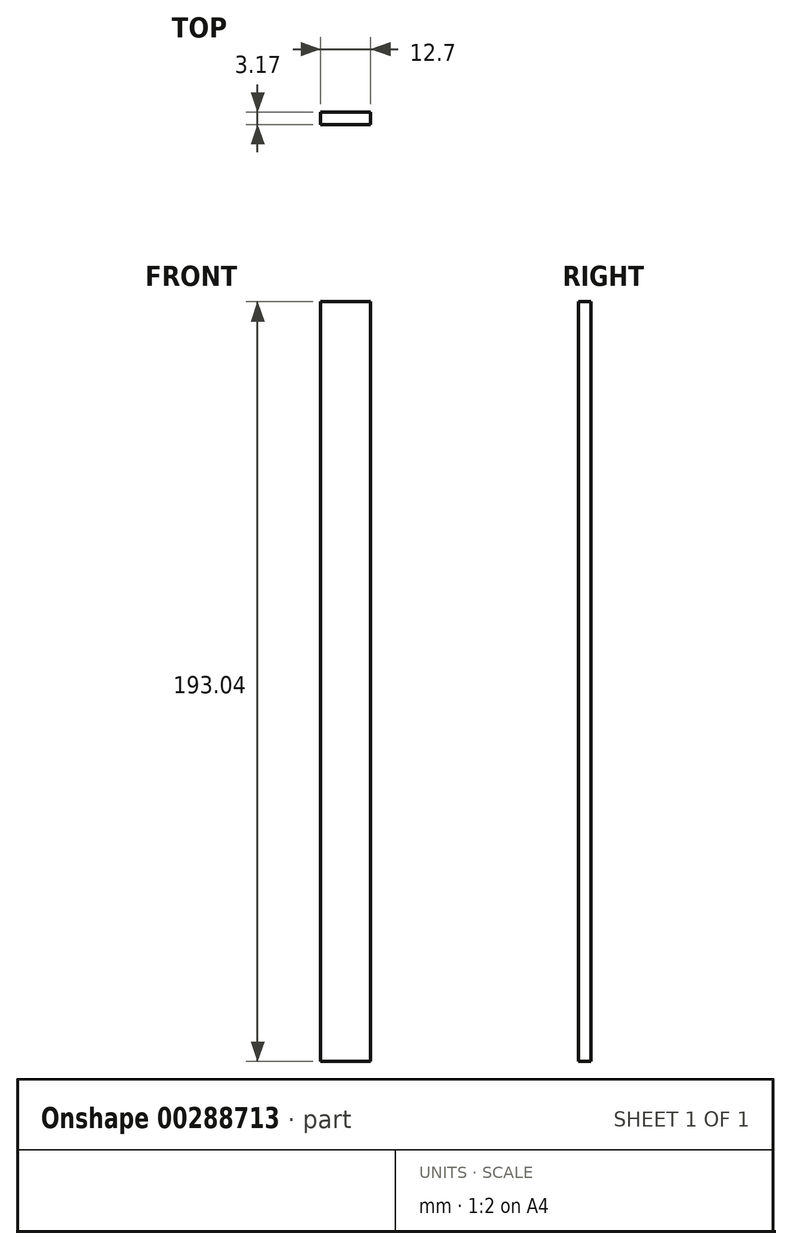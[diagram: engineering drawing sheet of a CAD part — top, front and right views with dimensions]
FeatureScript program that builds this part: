
annotation { "Feature Type Name" : "Feature", "Feature Type Description" : "" }
export const myFeature = defineFeature(function(context is Context, id is Id, definition is map)
    precondition{}
    {
        {
            var Q0;
            Q0=qCreatedBy(makeId("Front.planeOp"),FACE);
            var sketch = newSketch(context, id + "F0", { "sketchPlane" : qUnion([Q0])});
            skLineSegment(sketch, "E0.bottom", {"start": v(6.35, -96.52) * mm, "end": v(-6.35, -96.52) * mm});
            skLineSegment(sketch, "E0.top", {"start": v(6.35, 96.52) * mm, "end": v(-6.35, 96.52) * mm});
            skLineSegment(sketch, "E0.left", {"start": v(6.35, -96.52) * mm, "end": v(6.35, 96.52) * mm});
            skLineSegment(sketch, "E0.right", {"start": v(-6.35, -96.52) * mm, "end": v(-6.35, 96.52) * mm});
            skPoint(sketch, "E0.middle", {"position": v(0, 0) * mm});
            skSolve(sketch);
        }
        {
            var Q0;
            Q0=makeQuery(id+"F0.imprint","IMPRINT",FACE,{"disambiguationData":[TD([[makeQuery(id+"F0.imprint","IMPRINT",EDGE,{"derivedFrom":sQuery(id+"F0.wireOp",EDGE,"E0.bottom")}),-1.0]])]});
            extrude(context, id + "F1", {"entities" : qUnion([Q0]), "depth" : 3.17 * mm});
        }
    });
